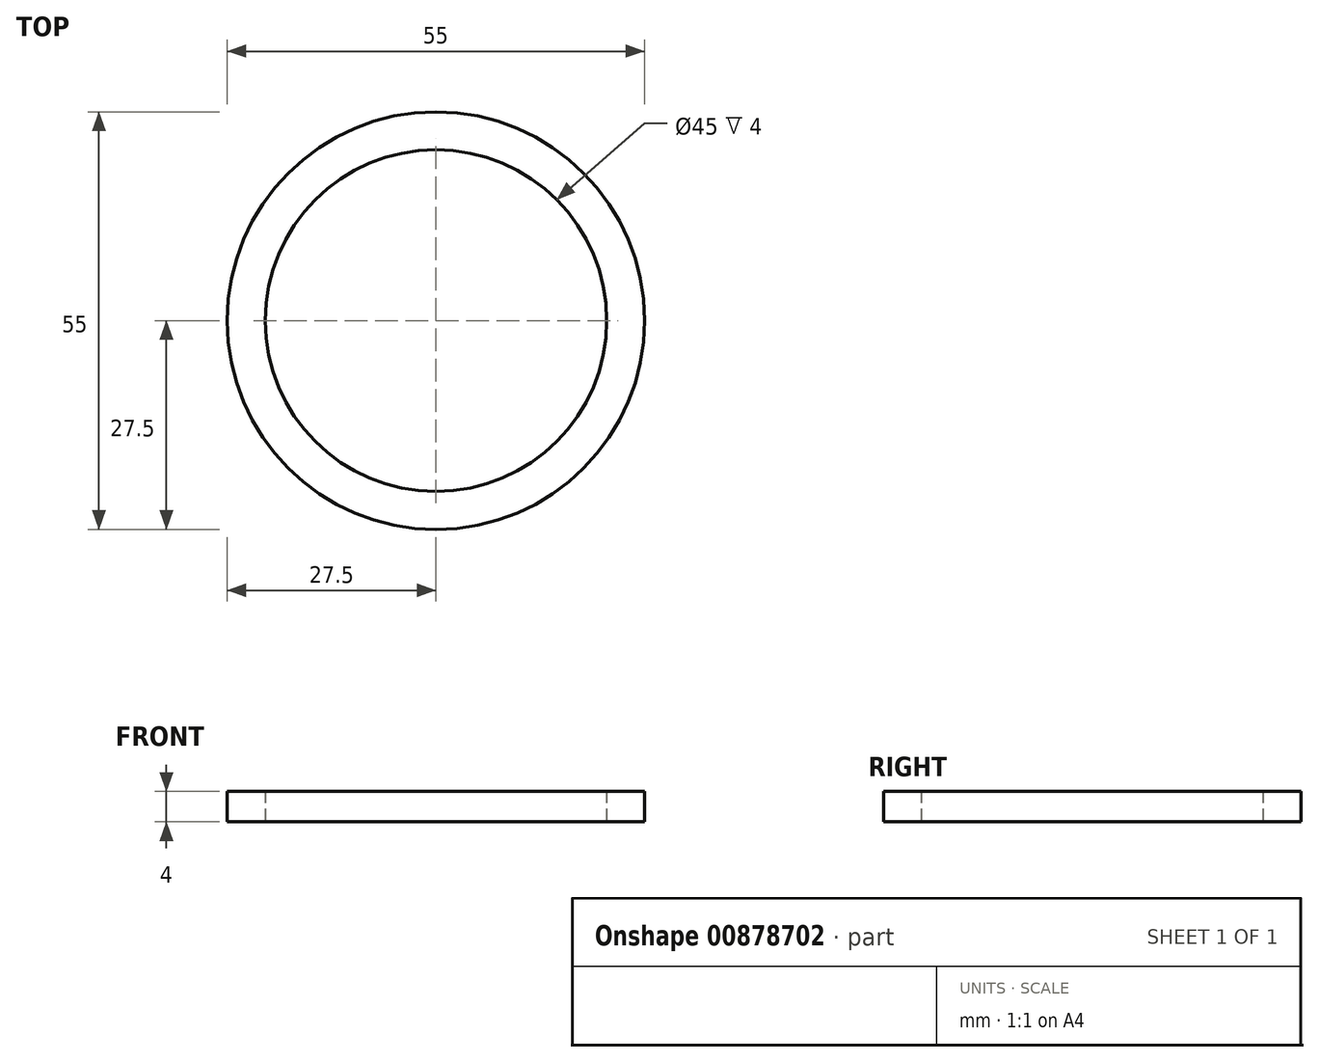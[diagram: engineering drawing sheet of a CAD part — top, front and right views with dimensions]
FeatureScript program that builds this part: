
annotation { "Feature Type Name" : "Feature", "Feature Type Description" : "" }
export const myFeature = defineFeature(function(context is Context, id is Id, definition is map)
    precondition{}
    {
        {
            var Q0;
            Q0=qCreatedBy(makeId("Top.planeOp"),FACE);
            var sketch = newSketch(context, id + "F0", { "sketchPlane" : qUnion([Q0])});
            skCircle(sketch, "E0", {"center": v(0, 0) * mm, "radius": 27.5 * mm});
            skCircle(sketch, "E1", {"center": v(0, 0) * mm, "radius": 22.5 * mm});
            skSolve(sketch);
        }
        {
            var Q0;
            Q0=makeQuery(id+"F0.imprint","IMPRINT",FACE,{"disambiguationData":[TD([[makeQuery(id+"F0.imprint","IMPRINT",EDGE,{"derivedFrom":sQuery(id+"F0.wireOp",EDGE,"E0")}),1.0]])]});
            extrude(context, id + "F1", {"entities" : qUnion([Q0]), "depth" : 4 * mm, "offsetDistance" : 25 * mm});
        }
    });
